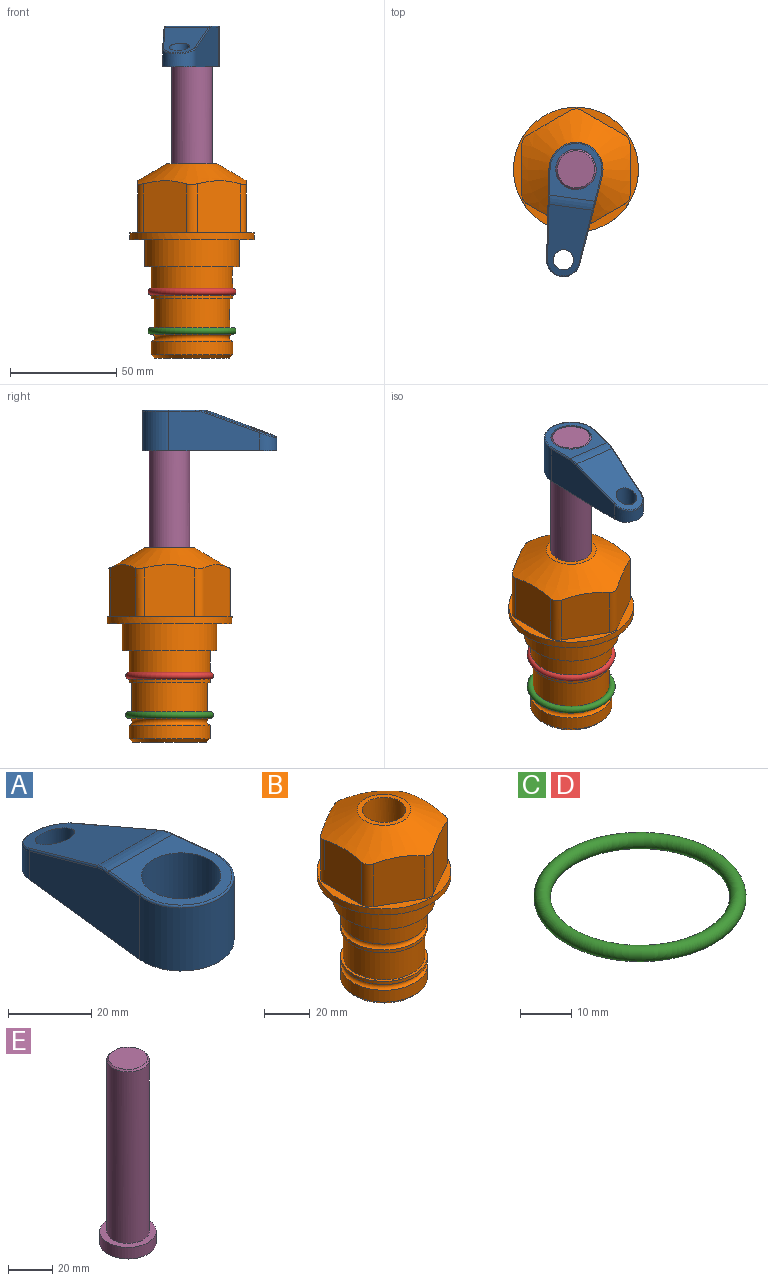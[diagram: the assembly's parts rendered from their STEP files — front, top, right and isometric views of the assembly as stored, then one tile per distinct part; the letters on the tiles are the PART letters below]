
ASSEMBLY  parts=5 mates=3
PART A: 44 faces, bbox 27.5x64.5x19.1 mm
  f0: plane 2.3x0.95mm, normal (0,0,-1), area 1mm2, adj f25,f30,f34
  f1: plane 63.5x25.4mm, normal (0,0,-1), area 561.7mm2, adj f2,f3,f4,f5,f6,f7,f19,f20
  f2: cylinder r=12.7mm len=25.4mm, axis (0,0,-1), area 792.2mm2, adj f1,f3,f5,f13
  f3: plane 42.33x18.54mm, normal (0.99,0.11,0), area 647mm2, adj f1,f2,f4,f11,f12,f14
  f4: cylinder r=7.94mm len=15.78mm, axis (0,0,-1), area 158.6mm2, adj f1,f3,f5,f16
  f5: plane 42.33x18.54mm, normal (-0.99,0.11,0), area 647mm2, adj f1,f2,f4,f15,f17,f18
  f6: cylinder r=9.53mm len=19.05mm, axis (0,0,-1), area 1140.1mm2, adj f1,f8
  f7: cylinder r=4.76mm len=10.98mm, axis (0,0,-1), area 276.1mm2, adj f1,f9
  f8: plane 25.83x24.38mm, normal (0,0,1), area 262.2mm2, adj f6,f10,f11,f13,f15
  f9: plane 32.49x20.55mm, normal (0,0.34,0.94), area 489.9mm2, adj f7,f10,f14,f16,f18
  f10: cylinder r=12.7mm len=21.49mm, axis (-1,0,0), area 93.2mm2, adj f8,f9,f12,f17
  f11: cylinder r=0.51mm len=12.34mm, axis (0.11,-0.99,0), area 9.9mm2, adj f3,f8,f12,f13
  f12: bspline ~7.62x1.64mm, area 3.5mm2, adj f3,f10,f11,f14
  f13: torus R=12.19mm, axis (0,0,1), area 33.6mm2, adj f2,f8,f11,f15
  f14: cylinder r=0.51mm len=26.01mm, axis (0.1,-0.93,0.34), area 21.6mm2, adj f3,f9,f12,f16
  f15: cylinder r=0.51mm len=12.34mm, axis (0.11,0.99,0), area 9.9mm2, adj f5,f8,f13,f17
  f16: bspline ~15.78x7.05mm, area 15.7mm2, adj f4,f9,f14,f18
  f17: bspline ~7.62x1.64mm, area 3.5mm2, adj f5,f10,f15,f18
  f18: cylinder r=0.51mm len=26.01mm, axis (0.1,0.93,-0.34), area 21.6mm2, adj f5,f9,f16,f17
  f19: plane 21.6x14.29mm, normal (-0.99,-0.11,0), area 242.6mm2, adj f1,f26,f28,f34,f36,f38
  f20: plane 21.6x14.29mm, normal (0.99,-0.11,0), area 242.6mm2, adj f1,f27,f29,f37,f39,f41
  f21: cylinder r=12.7mm len=14.29mm, axis (0,0,-1), area 173.2mm2, adj f1,f26,f27,f30,f31,f33
  f22: cylinder r=7.94mm len=7.63mm, axis (0,0,-1), area 53.8mm2, adj f1,f28,f29,f42
  f23: plane 2.3x0.95mm, normal (0,0,-1), area 1mm2, adj f25,f33,f37
  f24: plane 17.94x12.32mm, normal (0,-0.34,-0.94), area 191.2mm2, adj f25,f38,f41,f42
  f25: cylinder r=9.53mm len=12.93mm, axis (-1,0,0), area 37.5mm2, adj f0,f23,f24,f31,f36,f39
  f26: cylinder r=1.59mm len=14.29mm, axis (0,0,-1), area 49mm2, adj f1,f19,f21,f32
  f27: cylinder r=1.59mm len=14.29mm, axis (0,0,-1), area 49mm2, adj f1,f20,f21,f35
  f28: cylinder r=1.59mm len=7.28mm, axis (0,0,-1), area 22.1mm2, adj f1,f19,f22,f40
  f29: cylinder r=1.59mm len=7.28mm, axis (0,0,-1), area 22.1mm2, adj f1,f20,f22,f43
  f30: torus R=14.29mm, axis (0,0,1), area 5.8mm2, adj f0,f21,f31,f32
  f31: bspline ~11.06x2.73mm, area 20.8mm2, adj f21,f25,f30,f33
  f32: sphere r=1.59mm, area 5.4mm2, adj f26,f30,f34
  f33: torus R=14.29mm, axis (0,0,1), area 5.8mm2, adj f21,f23,f31,f35
  f34: cylinder r=1.59mm len=1.68mm, axis (-0.11,0.99,0), area 2.4mm2, adj f0,f19,f32,f36
  f35: sphere r=1.59mm, area 5.4mm2, adj f27,f33,f37
  f36: bspline ~5.82x2.33mm, area 7.7mm2, adj f19,f25,f34,f38
  f37: cylinder r=1.59mm len=1.68mm, axis (0.11,0.99,0), area 2.4mm2, adj f20,f23,f35,f39
  f38: cylinder r=1.59mm len=18.33mm, axis (0.1,-0.93,0.34), area 46.7mm2, adj f19,f24,f36,f40
  f39: bspline ~5.82x2.33mm, area 7.7mm2, adj f20,f25,f37,f41
  f40: sphere r=1.59mm, area 3.6mm2, adj f28,f38,f42
  f41: cylinder r=1.59mm len=18.33mm, axis (0.1,0.93,-0.34), area 46.7mm2, adj f20,f24,f39,f43
  f42: bspline ~8.31x1.84mm, area 15.3mm2, adj f22,f24,f40,f43
  f43: sphere r=1.59mm, area 3.6mm2, adj f29,f41,f42
PART B: 36 faces, bbox 58.7x58.7x91.2 mm
  f0: cylinder r=17.78mm len=35.56mm, axis (0,0,1), area 1670.8mm2, adj f23,f24,f31
  f1: cylinder r=19.05mm len=38.1mm, axis (0,0,1), area 1191.9mm2, adj f26,f27,f30
  f2: plane 58.66x58.66mm, normal (0,0,-1), area 1150.6mm2, adj f3,f28
  f3: cylinder r=29.33mm len=58.66mm, axis (0,0,-1), area 585.1mm2, adj f2,f4
  f4: plane 58.66x58.66mm, normal (0,0,1), area 475.9mm2, adj f3,f5,f6,f7,f8,f9,f10,f11
  f5: plane 24.5x20.32mm, normal (-0.5,0.87,0), area 562.8mm2, adj f4,f15,f16,f17
  f6: plane 24.5x20.32mm, normal (0.5,0.87,0), area 562.8mm2, adj f4,f14,f15,f17
  f7: plane 24.5x23.48mm, normal (1,0,0), area 562.8mm2, adj f4,f13,f14,f17
  f8: plane 24.5x20.32mm, normal (0.5,-0.87,0), area 562.8mm2, adj f4,f12,f13,f17
  f9: plane 24.5x20.32mm, normal (-0.5,-0.87,0), area 562.8mm2, adj f4,f11,f12,f17
  f10: plane 24.5x23.48mm, normal (-1,0,0), area 562.8mm2, adj f4,f11,f16,f17
  f11: cylinder r=5.08mm len=23.01mm, axis (0,0,-1), area 121.2mm2, adj f4,f9,f10,f17
  f12: cylinder r=5.08mm len=23.01mm, axis (0,0,-1), area 121.2mm2, adj f4,f8,f9,f17
  f13: cylinder r=5.08mm len=23.01mm, axis (0,0,-1), area 121.2mm2, adj f4,f7,f8,f17
  f14: cylinder r=5.08mm len=23.01mm, axis (0,0,-1), area 121.2mm2, adj f4,f6,f7,f17
  f15: cylinder r=5.08mm len=23.01mm, axis (0,0,-1), area 121.2mm2, adj f4,f5,f6,f17
  f16: cylinder r=5.08mm len=23.01mm, axis (0,0,-1), area 121.2mm2, adj f4,f5,f10,f17
  f17: cone r=11.73mm half-angle=60deg, axis (0,0,-1), area 2071.8mm2, adj f5,f6,f7,f8,f9,f10,f11,f12
  f18: plane 23.46x23.46mm, normal (0,0,1), area 147.4mm2, adj f17,f35
  f19: plane 34.93x34.93mm, normal (0,0,-1), area 958mm2, adj f29
  f20: cylinder r=19.05mm len=38.1mm, axis (0,0,1), area 760.1mm2, adj f21,f29
  f21: torus R=19.05mm, axis (0,0,1), area 565.3mm2, adj f20,f22
  f22: cylinder r=19.05mm len=38.1mm, axis (0,0,1), area 190mm2, adj f21,f23
  f23: plane 38.1x38.1mm, normal (0,0,1), area 146.9mm2, adj f0,f22
  f24: plane 38.1x38.1mm, normal (0,0,-1), area 146.9mm2, adj f0,f25
  f25: cylinder r=19.05mm len=38.1mm, axis (0,0,1), area 190mm2, adj f24,f26
  f26: torus R=19.05mm, axis (0,0,1), area 565.3mm2, adj f1,f25
  f27: plane 44.45x44.45mm, normal (0,0,-1), area 411.7mm2, adj f1,f28
  f28: cylinder r=22.23mm len=44.45mm, axis (0,0,1), area 1773.5mm2, adj f2,f27
  f29: cone r=19.05mm half-angle=45deg, axis (0,0,1), area 257.5mm2, adj f19,f20
  f30: cylinder r=3.17mm len=6.75mm, axis (-1,0,0), area 128mm2, adj f1,f33
  f31: cylinder r=3.17mm len=6.35mm, axis (-1,0,0), area 102.5mm2, adj f0,f33
  f32: plane 25.4x25.4mm, normal (0,0,1), area 506.7mm2, adj f33
  f33: cylinder r=12.7mm len=66.42mm, axis (0,0,-1), area 5236.2mm2, adj f30,f31,f32,f34
  f34: cone r=9.53mm half-angle=30deg, axis (0,0,-1), area 443.4mm2, adj f33,f35
  f35: cylinder r=9.53mm len=19.05mm, axis (0,0,-1), area 849mm2, adj f18,f34
PART C: 1 faces, bbox 44.7x44.7x3.2 mm
  f0: torus R=19.05mm, axis (0,0,1), area 1193.9mm2
PART D: same geometry as C
PART E: 6 faces, bbox 25.4x25.4x101.6 mm
  f0: plane 17.46x17.46mm, normal (0,0,1), area 239.5mm2, adj f5
  f1: plane 25.4x25.4mm, normal (0,0,-1), area 506.7mm2, adj f2
  f2: cylinder r=12.7mm len=25.4mm, axis (0,0,1), area 506.7mm2, adj f1,f3
  f3: plane 25.4x25.4mm, normal (0,0,1), area 221.7mm2, adj f2,f4
  f4: cylinder r=9.53mm len=94.46mm, axis (0,0,1), area 5653mm2, adj f3,f5
  f5: cone r=8.73mm half-angle=45deg, axis (0,0,-1), area 64.4mm2, adj f0,f4
PLACE A rot(axis=(0,0,1),172.1deg) t=(0,0,81.24)mm
PLACE B at identity fixed
PLACE C t=(0,0,-18.41)mm
PLACE D at identity
PLACE E rot(axis=(0,0,1),172.1deg) t=(0,0,26.63)mm
MATE fastened A.f2 <-> E.f2  axis (0,0,-1) through (0,0,100.29)mm
MATE cylindrical E.f2 <-> B.f0  axis (0,0,1) through (0,0,52.27)mm
MATE fastened C.f0 <-> B.f0  axis (0,0,1) through (0,0,-42.93)mm
